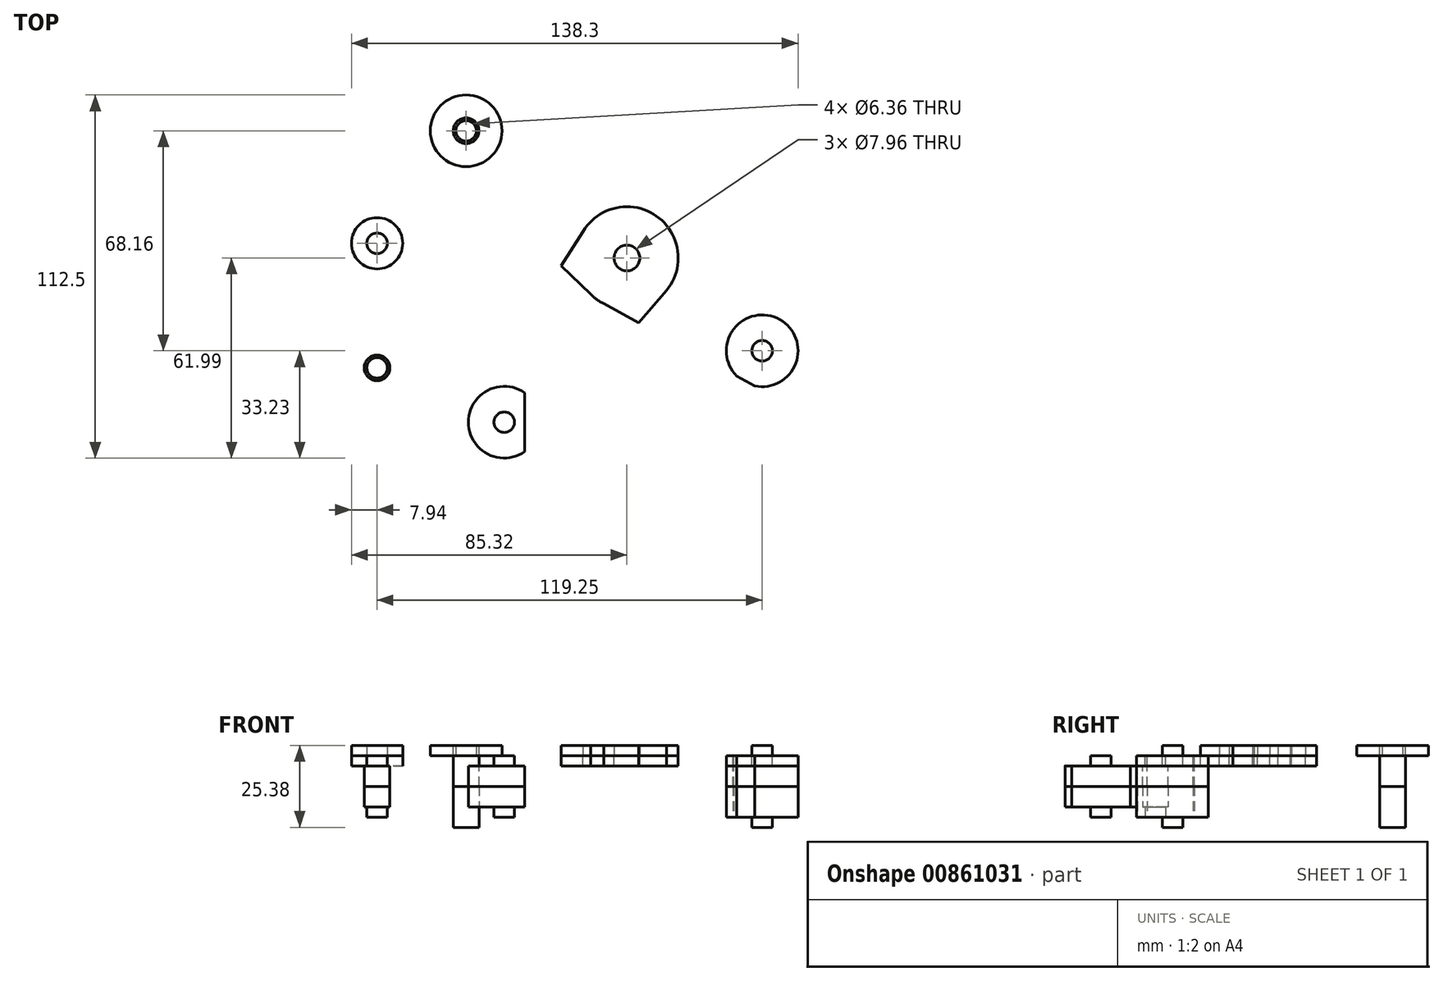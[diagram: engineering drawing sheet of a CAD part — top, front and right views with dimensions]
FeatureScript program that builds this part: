
annotation { "Feature Type Name" : "Feature", "Feature Type Description" : "" }
export const myFeature = defineFeature(function(context is Context, id is Id, definition is map)
    precondition{}
    {
        {
            var Q0;
            Q0=qCreatedBy(makeId("Top.planeOp"),FACE);
            var sketch = newSketch(context, id + "F0", { "sketchPlane" : qUnion([Q0])});
            skLineSegment(sketch, "E0", {"start": v(-49.8, 39.4) * mm, "end": v(0, 0) * mm, "construction": true});
            skLineSegment(sketch, "E1", {"start": v(0, 0) * mm, "end": v(41.87, -28.76) * mm, "construction": true});
            skLineSegment(sketch, "E2", {"start": v(-49.8, 39.4) * mm, "end": v(-77.38, 4.55) * mm, "construction": true});
            skLineSegment(sketch, "E3", {"start": v(-77.38, 4.55) * mm, "end": v(-77.38, -14.63) * mm, "construction": true});
            skPoint(sketch, "E4.orphan", {"position": v(-49.8, -7.7) * mm});
            skCircle(sketch, "E5", {"center": v(0, 0) * mm, "radius": 3.18 * mm});
            skCircle(sketch, "E6", {"center": v(0, 0) * mm, "radius": 3.98 * mm});
            skCircle(sketch, "E7", {"center": v(0, 0) * mm, "radius": 15.88 * mm});
            skCircle(sketch, "E8", {"center": v(41.87, -28.76) * mm, "radius": 3.18 * mm});
            skCircle(sketch, "E9", {"center": v(41.87, -28.76) * mm, "radius": 11.11 * mm});
            skCircle(sketch, "E10", {"center": v(-49.8, 39.4) * mm, "radius": 11.11 * mm});
            skCircle(sketch, "E11", {"center": v(-49.8, 39.4) * mm, "radius": 3.18 * mm});
            skCircle(sketch, "E12", {"center": v(-77.38, 4.55) * mm, "radius": 3.18 * mm});
            skCircle(sketch, "E13", {"center": v(-77.38, 4.55) * mm, "radius": 7.94 * mm});
            skCircle(sketch, "E14", {"center": v(30.4, -20.26) * mm, "radius": 3.18 * mm});
            skPoint(sketch, "E15.endSnap0", {"position": v(-38, -50.88) * mm});
            skCircle(sketch, "E16", {"center": v(-38, -50.88) * mm, "radius": 3.18 * mm});
            skCircle(sketch, "E17", {"center": v(-38, -50.88) * mm, "radius": 11.11 * mm});
            skCircle(sketch, "E18", {"center": v(-77.38, -34.04) * mm, "radius": 3.18 * mm});
            skCircle(sketch, "E19", {"center": v(-77.38, -34.04) * mm, "radius": 7.94 * mm});
            skLineSegment(sketch, "E20", {"start": v(-83.41, 9.7) * mm, "end": v(-58.99, 45.65) * mm});
            skLineSegment(sketch, "E21", {"start": v(-42.1, 47.42) * mm, "end": v(8.86, 13.18) * mm});
            skLineSegment(sketch, "E22", {"start": v(11.66, 10.77) * mm, "end": v(48.97, -20.21) * mm});
            skLineSegment(sketch, "E23", {"start": v(39.63, -39.65) * mm, "end": v(-7.59, -13.94) * mm});
            skLineSegment(sketch, "E24", {"start": v(-11.02, -11.43) * mm, "end": v(-40.12, 16.62) * mm});
            skLineSegment(sketch, "E25", {"start": v(-70.87, 0) * mm, "end": v(-55.97, 16.24) * mm});
            skLineSegment(sketch, "E26", {"start": v(0, 0) * mm, "end": v(-38, -50.88) * mm, "construction": true});
            skCircle(sketch, "E27", {"center": v(-25.64, -34.33) * mm, "radius": 3.18 * mm});
            skLineSegment(sketch, "E28", {"start": v(-43.85, -60.32) * mm, "end": v(-81.03, -41.1) * mm});
            skLineSegment(sketch, "E29", {"start": v(-76.2, -26.2) * mm, "end": v(-50.23, -35) * mm});
            skArc(sketch, "E30", {"start": v(-40.12, 16.62) * mm, "mid": v(-48.22, 23.74) * mm, "end": v(-55.97, 16.24) * mm});
            skArc(sketch, "E31", {"start": v(-50.23, -35) * mm, "mid": v(-44.3, -36) * mm, "end": v(-39.37, -32.55) * mm});
            skLineSegment(sketch, "E32.trimOffspring", {"start": v(-41.6, 31.9) * mm, "end": v(-41.06, 32.49) * mm});
            skLineSegment(sketch, "E33.trimOffspring", {"start": v(-49.15, 23.67) * mm, "end": v(-48.34, 24.55) * mm});
            skLineSegment(sketch, "E34.trimOffspring", {"start": v(-47.5, 23.73) * mm, "end": v(-48.34, 24.55) * mm});
            skLineSegment(sketch, "E35", {"start": v(-39.37, -32.55) * mm, "end": v(-13.42, 8.48) * mm});
            skLineSegment(sketch, "E36", {"start": v(-28.87, -57.22) * mm, "end": v(13.17, -9.05) * mm});
            skSolve(sketch);
        }
        {
            var Q0;
            Q0=makeQuery(id+"F0.imprint","IMPRINT",FACE,{"disambiguationData":[TD([[makeQuery(id+"F0.imprint","IMPRINT",EDGE,{"derivedFrom":sQuery(id+"F0.wireOp",EDGE,"E12")}),-1.0]])]});
            var Q1;
            {var subQ8=sQuery(id+"F0.wireOp",EDGE,"E20");Q1=makeQuery(id+"F0.imprint","IMPRINT",FACE,{"disambiguationData":[TD([[makeQuery(id+"F0.imprint","IMPRINT",EDGE,{"derivedFrom":subQ8}),-1.0]])]});}
            var Q2;
            Q2=makeQuery(id+"F0.imprint","IMPRINT",FACE,{"disambiguationData":[TD([[makeQuery(id+"F0.imprint","IMPRINT",EDGE,{"derivedFrom":sQuery(id+"F0.wireOp",EDGE,"E11")}),-1.0]])]});
            var Q3;
            Q3=makeQuery(id+"F0.imprint","IMPRINT",FACE,{"disambiguationData":[TD([[makeQuery(id+"F0.imprint","IMPRINT",EDGE,{"derivedFrom":sQuery(id+"F0.wireOp",EDGE,"E6")}),-1.0]])]});
            var Q4;
            {var subQ0=sQuery(id+"F0.wireOp",EDGE,"E24");var subQ1=sQuery(id+"F0.wireOp",EDGE,"E7");var subQ2=makeQuery(id+"F0.imprint","INTERSECT",VERTEX,{"derivedFrom":[subQ1,subQ0]});Q4=makeQuery(id+"F0.imprint","IMPRINT",FACE,{"disambiguationData":[TD([[makeQuery(id+"F0.imprint","IMPRINT",EDGE,{"disambiguationData":[TD([[subQ2,1.0]])],"derivedFrom":subQ1}),-1.0]])]});}
            var Q5;
            {var subQ0=sQuery(id+"F0.wireOp",EDGE,"E23");var subQ1=sQuery(id+"F0.wireOp",EDGE,"E7");var subQ2=makeQuery(id+"F0.imprint","INTERSECT",VERTEX,{"derivedFrom":[subQ1,subQ0]});Q5=makeQuery(id+"F0.imprint","IMPRINT",FACE,{"disambiguationData":[TD([[makeQuery(id+"F0.imprint","IMPRINT",EDGE,{"disambiguationData":[TD([[subQ2,-1.0]])],"derivedFrom":subQ1}),-1.0]])]});}
            var Q6;
            {var subQ0=sQuery(id+"F0.wireOp",EDGE,"E14");Q6=makeQuery(id+"F0.imprint","IMPRINT",FACE,{"disambiguationData":[TD([[makeQuery(id+"F0.imprint","IMPRINT",EDGE,{"derivedFrom":subQ0}),-1.0]])]});}
            var Q7;
            Q7=makeQuery(id+"F0.imprint","IMPRINT",FACE,{"disambiguationData":[TD([[makeQuery(id+"F0.imprint","IMPRINT",EDGE,{"derivedFrom":sQuery(id+"F0.wireOp",EDGE,"E8")}),-1.0]])]});
            extrude(context, id + "F1", {"entities" : qUnion([Q0, Q1, Q2, Q3, Q4, Q5, Q6, Q7]), "depth" : 3.17 * mm, "offsetDistance" : 25.4 * mm});
        }
        {
            var Q0;
            Q0=makeQuery(id+"F0.imprint","IMPRINT",FACE,{"disambiguationData":[TD([[makeQuery(id+"F0.imprint","IMPRINT",EDGE,{"derivedFrom":sQuery(id+"F0.wireOp",EDGE,"E27")}),-1.0]])]});
            var Q1;
            Q1=makeQuery(id+"F0.imprint","IMPRINT",FACE,{"disambiguationData":[TD([[makeQuery(id+"F0.imprint","IMPRINT",EDGE,{"derivedFrom":sQuery(id+"F0.wireOp",EDGE,"E16")}),-1.0]])]});
            var Q2;
            Q2=makeQuery(id+"F0.imprint","IMPRINT",FACE,{"disambiguationData":[TD([[makeQuery(id+"F0.imprint","IMPRINT",EDGE,{"derivedFrom":sQuery(id+"F0.wireOp",EDGE,"E18")}),-1.0]])]});
            var Q3;
            Q3=makeQuery(id+"F0.imprint","IMPRINT",FACE,{"disambiguationData":[TD([[makeQuery(id+"F0.imprint","IMPRINT",EDGE,{"derivedFrom":sQuery(id+"F0.wireOp",EDGE,"E6")}),-1.0]])]});
            var Q4;
            {var subQ0=sQuery(id+"F0.wireOp",EDGE,"E23");var subQ1=sQuery(id+"F0.wireOp",EDGE,"E7");var subQ2=makeQuery(id+"F0.imprint","INTERSECT",VERTEX,{"derivedFrom":[subQ1,subQ0]});Q4=makeQuery(id+"F0.imprint","IMPRINT",FACE,{"disambiguationData":[TD([[makeQuery(id+"F0.imprint","IMPRINT",EDGE,{"disambiguationData":[TD([[subQ2,-1.0]])],"derivedFrom":subQ1}),-1.0]])]});}
            var Q5;
            {var subQ0=sQuery(id+"F0.wireOp",EDGE,"E24");var subQ1=sQuery(id+"F0.wireOp",EDGE,"E7");var subQ2=makeQuery(id+"F0.imprint","INTERSECT",VERTEX,{"derivedFrom":[subQ1,subQ0]});Q5=makeQuery(id+"F0.imprint","IMPRINT",FACE,{"disambiguationData":[TD([[makeQuery(id+"F0.imprint","IMPRINT",EDGE,{"disambiguationData":[TD([[subQ2,1.0]])],"derivedFrom":subQ1}),-1.0]])]});}
            extrude(context, id + "F2", {"entities" : qUnion([Q0, Q1, Q2, Q3, Q4, Q5]), "oppositeDirection" : true, "depth" : 3.17 * mm, "offsetDistance" : 25.4 * mm});
        }
        {
            var Q0;
            Q0=makeQuery(id+"F1.opExtrude","CAP_FACE",FACE,{"disambiguationData":[OSD([sQuery(id+"F0.wireOp",EDGE,"E6"),sQuery(id+"F0.wireOp",EDGE,"E7"),sQuery(id+"F0.wireOp",EDGE,"E8"),sQuery(id+"F0.wireOp",EDGE,"E9"),sQuery(id+"F0.wireOp",EDGE,"E10"),sQuery(id+"F0.wireOp",EDGE,"E11"),sQuery(id+"F0.wireOp",EDGE,"E12"),sQuery(id+"F0.wireOp",EDGE,"E13"),sQuery(id+"F0.wireOp",EDGE,"E14"),sQuery(id+"F0.wireOp",EDGE,"E20"),sQuery(id+"F0.wireOp",EDGE,"E21"),sQuery(id+"F0.wireOp",EDGE,"E22"),sQuery(id+"F0.wireOp",EDGE,"E23"),sQuery(id+"F0.wireOp",EDGE,"E24"),sQuery(id+"F0.wireOp",EDGE,"E25"),sQuery(id+"F0.wireOp",EDGE,"E30"),sQuery(id+"F0.wireOp",EDGE,"E33.trimOffspring"),sQuery(id+"F0.wireOp",EDGE,"E34.trimOffspring")])],"isStart":false});
            var sketch = newSketch(context, id + "F3", { "sketchPlane" : qUnion([Q0])});
            skCircle(sketch, "E37", {"center": v(-49.8, 39.4) * mm, "radius": 3.98 * mm});
            skCircle(sketch, "E38", {"center": v(0, 0) * mm, "radius": 3.98 * mm});
            skCircle(sketch, "E39", {"center": v(41.87, -28.76) * mm, "radius": 11.11 * mm});
            skSolve(sketch);
        }
        {
            var Q0;
            Q0=makeQuery(id+"F2.opExtrude","CAP_FACE",FACE,{"disambiguationData":[OSD([sQuery(id+"F0.wireOp",EDGE,"E7"),sQuery(id+"F0.wireOp",EDGE,"E16"),sQuery(id+"F0.wireOp",EDGE,"E17"),sQuery(id+"F0.wireOp",EDGE,"E18"),sQuery(id+"F0.wireOp",EDGE,"E19"),sQuery(id+"F0.wireOp",EDGE,"E23"),sQuery(id+"F0.wireOp",EDGE,"E24"),sQuery(id+"F0.wireOp",EDGE,"E27"),sQuery(id+"F0.wireOp",EDGE,"E28"),sQuery(id+"F0.wireOp",EDGE,"E29"),sQuery(id+"F0.wireOp",EDGE,"E31"),sQuery(id+"F0.wireOp",EDGE,"E35"),sQuery(id+"F0.wireOp",EDGE,"E36")])],"isStart":true});
            var sketch = newSketch(context, id + "F4", { "sketchPlane" : qUnion([Q0])});
            skCircle(sketch, "E40", {"center": v(-38, -50.88) * mm, "radius": 11.11 * mm});
            skCircle(sketch, "E41", {"center": v(-77.38, -34.04) * mm, "radius": 3.98 * mm});
            skLineSegment(sketch, "E42", {"start": v(-31.64, -41.76) * mm, "end": v(-31.64, -60) * mm});
            skSolve(sketch);
        }
        {
            var Q0;
            Q0=qCreatedBy(makeId("Top.planeOp"),FACE);
            cPlane(context, id + "F5", {"entities" : qUnion([Q0]), "cplaneType" : CPlaneType.OFFSET, "offset" : 9.52 * mm, "oppositeDirection" : true, "width" : 152.4 * mm, "height" : 152.4 * mm});
        }
        {
            var Q0;
            Q0=makeQuery(id+"F3.imprint","IMPRINT",FACE,{"disambiguationData":[TD([[makeQuery(id+"F3.imprint","IMPRINT",EDGE,{"derivedFrom":sQuery(id+"F3.wireOp",EDGE,"E37")}),1.0]])]});
            var Q1;
            Q1=makeQuery(id+"F4.imprint","IMPRINT",FACE,{"disambiguationData":[TD([[makeQuery(id+"F4.imprint","IMPRINT",EDGE,{"derivedFrom":sQuery(id+"F4.wireOp",EDGE,"E41")}),1.0]])]});
            var Q2;
            {var subQ2=sQuery(id+"F4.wireOp",EDGE,"E42");Q2=makeQuery(id+"F4.imprint","IMPRINT",FACE,{"disambiguationData":[TD([[makeQuery(id+"F4.imprint","IMPRINT",EDGE,{"derivedFrom":subQ2}),-1.0]])]});}
            var Q3;
            Q3=makeQuery(id+"F3.imprint","IMPRINT",FACE,{"disambiguationData":[TD([[makeQuery(id+"F3.imprint","IMPRINT",EDGE,{"derivedFrom":makeQuery(id+"F1.opExtrude","CAP_EDGE",EDGE,{"disambiguationData":[OSD([sQuery(id+"F0.wireOp",EDGE,"E8")])],"isStart":false})}),-1.0]])]});
            var Q4;
            Q4=makeQuery(id+"F3.imprint","IMPRINT",FACE,{"disambiguationData":[TD([[makeQuery(id+"F3.imprint","IMPRINT",EDGE,{"derivedFrom":makeQuery(id+"F1.opExtrude","CAP_EDGE",EDGE,{"disambiguationData":[OSD([sQuery(id+"F0.wireOp",EDGE,"E11")])],"isStart":false})}),1.0]])]});
            var Q5;
            Q5=makeQuery(id+"F4.imprint","IMPRINT",FACE,{"disambiguationData":[TD([[makeQuery(id+"F4.imprint","IMPRINT",EDGE,{"derivedFrom":makeQuery(id+"F2.opExtrude","CAP_EDGE",EDGE,{"disambiguationData":[OSD([sQuery(id+"F0.wireOp",EDGE,"E18")])],"isStart":true})}),1.0]])]});
            var Q6;
            Q6=makeQuery(id+"F3.imprint","IMPRINT",FACE,{"disambiguationData":[TD([[makeQuery(id+"F3.imprint","IMPRINT",EDGE,{"derivedFrom":makeQuery(id+"F1.opExtrude","CAP_EDGE",EDGE,{"disambiguationData":[OSD([sQuery(id+"F0.wireOp",EDGE,"E8")])],"isStart":false})}),1.0]])]});
            var Q7;
            Q7=makeQuery(id+"F4.imprint","IMPRINT",FACE,{"disambiguationData":[TD([[makeQuery(id+"F4.imprint","IMPRINT",EDGE,{"derivedFrom":makeQuery(id+"F2.opExtrude","CAP_EDGE",EDGE,{"disambiguationData":[OSD([sQuery(id+"F0.wireOp",EDGE,"E16")])],"isStart":true})}),1.0]])]});
            var Q8;
            Q8=qCreatedBy(id+"F5.planeOp",FACE);
            extrude(context, id + "F6", {"entities" : qUnion([Q0, Q1, Q2, Q3, Q4, Q5, Q6, Q7]), "endBound" : BoundingType.UP_TO_SURFACE, "oppositeDirection" : true, "depth" : 25.4 * mm, "endBoundEntityFace" : qUnion([Q8]), "offsetDistance" : 25.4 * mm});
        }
        {
            var Q0;
            Q0=makeQuery(id+"F1.opExtrude","SWEPT_BODY",BODY,{"disambiguationData":[OSD([sQuery(id+"F0.wireOp",EDGE,"E6"),sQuery(id+"F0.wireOp",EDGE,"E7"),sQuery(id+"F0.wireOp",EDGE,"E8"),sQuery(id+"F0.wireOp",EDGE,"E9"),sQuery(id+"F0.wireOp",EDGE,"E10"),sQuery(id+"F0.wireOp",EDGE,"E11"),sQuery(id+"F0.wireOp",EDGE,"E12"),sQuery(id+"F0.wireOp",EDGE,"E13"),sQuery(id+"F0.wireOp",EDGE,"E14"),sQuery(id+"F0.wireOp",EDGE,"E20"),sQuery(id+"F0.wireOp",EDGE,"E21"),sQuery(id+"F0.wireOp",EDGE,"E22"),sQuery(id+"F0.wireOp",EDGE,"E23"),sQuery(id+"F0.wireOp",EDGE,"E24"),sQuery(id+"F0.wireOp",EDGE,"E25"),sQuery(id+"F0.wireOp",EDGE,"E30"),sQuery(id+"F0.wireOp",EDGE,"E33.trimOffspring"),sQuery(id+"F0.wireOp",EDGE,"E34.trimOffspring")])]});
            var Q1;
            Q1=makeQuery(id+"F2.opExtrude","SWEPT_BODY",BODY,{"disambiguationData":[OSD([sQuery(id+"F0.wireOp",EDGE,"E6"),sQuery(id+"F0.wireOp",EDGE,"E7"),sQuery(id+"F0.wireOp",EDGE,"E16"),sQuery(id+"F0.wireOp",EDGE,"E17"),sQuery(id+"F0.wireOp",EDGE,"E18"),sQuery(id+"F0.wireOp",EDGE,"E19"),sQuery(id+"F0.wireOp",EDGE,"E27"),sQuery(id+"F0.wireOp",EDGE,"E28"),sQuery(id+"F0.wireOp",EDGE,"E29"),sQuery(id+"F0.wireOp",EDGE,"E31"),sQuery(id+"F0.wireOp",EDGE,"E35"),sQuery(id+"F0.wireOp",EDGE,"E36")])]});
            var Q2;
            Q2=makeQuery(id+"F6.opExtrude","SWEPT_BODY",BODY,{"disambiguationData":[OSD([sQuery(id+"F3.wireOp",EDGE,"E37")])]});
            var Q3;
            Q3=makeQuery(id+"F6.opExtrude","SWEPT_BODY",BODY,{"disambiguationData":[OSD([sQuery(id+"F0.wireOp",EDGE,"E23"),sQuery(id+"F3.wireOp",EDGE,"E39")])]});
            var Q4;
            Q4=makeQuery(id+"F6.opExtrude","SWEPT_BODY",BODY,{"disambiguationData":[OSD([sQuery(id+"F4.wireOp",EDGE,"E40"),sQuery(id+"F4.wireOp",EDGE,"E42")])]});
            var Q5;
            Q5=makeQuery(id+"F6.opExtrude","SWEPT_BODY",BODY,{"disambiguationData":[OSD([sQuery(id+"F4.wireOp",EDGE,"E41")])]});
            booleanBodies(context, id + "F7", {"operationType" : BooleanOperationType.SUBTRACTION, "tools" : qUnion([Q0, Q1]), "targets" : qUnion([Q2, Q3, Q4, Q5])});
        }
        {
            var Q0;
            Q0=makeQuery(id+"F6.opExtrude","SWEPT_BODY",BODY,{"disambiguationData":[OSD([sQuery(id+"F0.wireOp",EDGE,"E23"),sQuery(id+"F3.wireOp",EDGE,"E39")])]});
            var Q1;
            Q1=makeQuery(id+"F6.opExtrude","SWEPT_BODY",BODY,{"disambiguationData":[OSD([sQuery(id+"F4.wireOp",EDGE,"E40"),sQuery(id+"F4.wireOp",EDGE,"E42")])]});
            var Q2;
            Q2=makeQuery(id+"F6.opExtrude","SWEPT_BODY",BODY,{"disambiguationData":[OSD([sQuery(id+"F4.wireOp",EDGE,"E41")])]});
            var Q3;
            Q3=makeQuery(id+"F6.opExtrude","SWEPT_BODY",BODY,{"disambiguationData":[OSD([sQuery(id+"F3.wireOp",EDGE,"E37")])]});
            var Q4;
            Q4=qCreatedBy(id+"F5.planeOp",FACE);
            mirror(context, id + "F8", {"entities" : qUnion([Q0, Q1, Q2, Q3]), "mirrorPlane" : qUnion([Q4])});
        }
        {
            var Q0;
            {var subQ0=sQuery(id+"F0.wireOp",EDGE,"E14");Q0=makeQuery(id+"F0.imprint","IMPRINT",FACE,{"disambiguationData":[TD([[makeQuery(id+"F0.imprint","IMPRINT",EDGE,{"derivedFrom":subQ0}),-1.0]])]});}
            var Q1;
            Q1=makeQuery(id+"F0.imprint","IMPRINT",FACE,{"disambiguationData":[TD([[makeQuery(id+"F0.imprint","IMPRINT",EDGE,{"derivedFrom":sQuery(id+"F0.wireOp",EDGE,"E6")}),-1.0]])]});
            var Q2;
            {var subQ0=sQuery(id+"F0.wireOp",EDGE,"E24");var subQ1=sQuery(id+"F0.wireOp",EDGE,"E7");var subQ2=makeQuery(id+"F0.imprint","INTERSECT",VERTEX,{"derivedFrom":[subQ1,subQ0]});Q2=makeQuery(id+"F0.imprint","IMPRINT",FACE,{"disambiguationData":[TD([[makeQuery(id+"F0.imprint","IMPRINT",EDGE,{"disambiguationData":[TD([[subQ2,1.0]])],"derivedFrom":subQ1}),-1.0]])]});}
            var Q3;
            {var subQ0=sQuery(id+"F0.wireOp",EDGE,"E23");var subQ1=sQuery(id+"F0.wireOp",EDGE,"E7");var subQ2=makeQuery(id+"F0.imprint","INTERSECT",VERTEX,{"derivedFrom":[subQ1,subQ0]});Q3=makeQuery(id+"F0.imprint","IMPRINT",FACE,{"disambiguationData":[TD([[makeQuery(id+"F0.imprint","IMPRINT",EDGE,{"disambiguationData":[TD([[subQ2,-1.0]])],"derivedFrom":subQ1}),-1.0]])]});}
            var Q4;
            {var subQ8=sQuery(id+"F0.wireOp",EDGE,"E20");Q4=makeQuery(id+"F0.imprint","IMPRINT",FACE,{"disambiguationData":[TD([[makeQuery(id+"F0.imprint","IMPRINT",EDGE,{"derivedFrom":subQ8}),-1.0]])]});}
            var Q5;
            Q5=makeQuery(id+"F0.imprint","IMPRINT",FACE,{"disambiguationData":[TD([[makeQuery(id+"F0.imprint","IMPRINT",EDGE,{"derivedFrom":sQuery(id+"F0.wireOp",EDGE,"E12")}),-1.0]])]});
            extrude(context, id + "F9", {"entities" : qUnion([Q0, Q1, Q2, Q3, Q4, Q5]), "oppositeDirection" : true, "depth" : 3.17 * mm, "offsetDistance" : 25.4 * mm});
        }
    });
